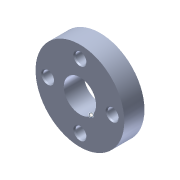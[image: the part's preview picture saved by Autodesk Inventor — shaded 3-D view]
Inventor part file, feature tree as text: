
AUTODESK INVENTOR PART (.ipt)
format: ipt  version: 2013 (Build 170138000, 138)  size: 121,344 bytes
history: native  units: in
note: dims shown in document units (in); Inventor stores cm internally (conversion verified against a paired STEP export)
features: extrude x1, other x1, imported_body x1
ambient origin geometry x8: Origin, YZ Plane, XZ Plane, XY Plane, X Axis, Y Axis, Z Axis, Center Point
feature tree (3):
  extrude  "Extrude2"  TaperAngle=0.0deg  [1 undecoded]
  other  "User Library-Omni wheel joining hub1"
  imported_body  "Base1"
note: 1 required parameter value undecoded (feature->parameter linkage not recoverable at this tier; creation-order binding heuristic only, values carry confidence <= 0.55)
